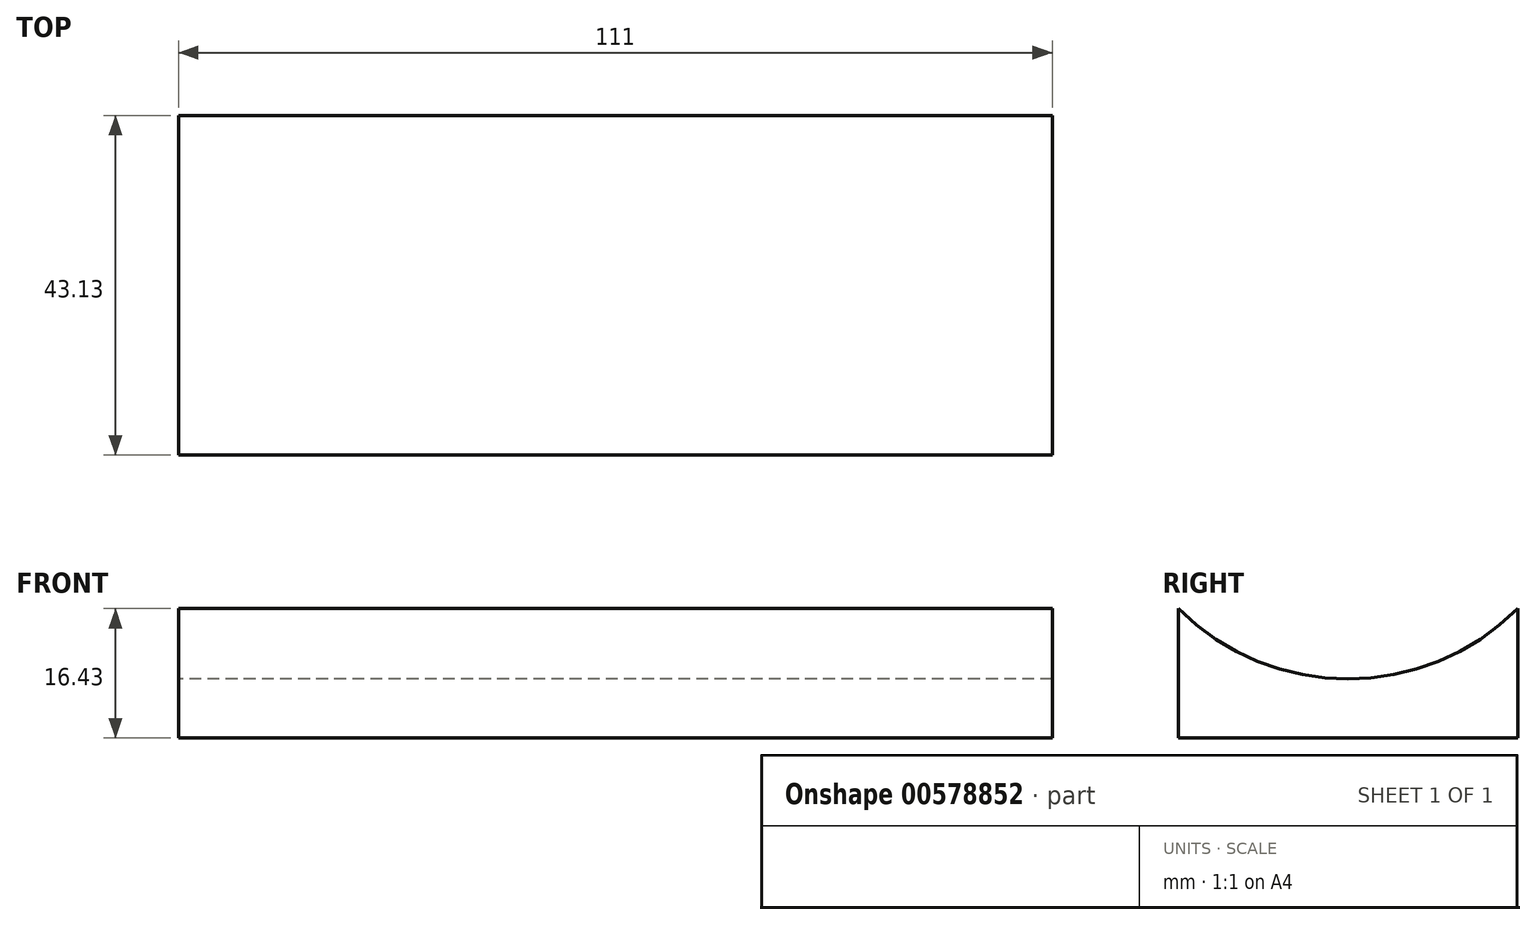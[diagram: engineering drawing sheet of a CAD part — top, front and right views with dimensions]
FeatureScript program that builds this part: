
annotation { "Feature Type Name" : "Feature", "Feature Type Description" : "" }
export const myFeature = defineFeature(function(context is Context, id is Id, definition is map)
    precondition{}
    {
        {
            var Q0;
            Q0=qCreatedBy(makeId("Right.planeOp"),FACE);
            var sketch = newSketch(context, id + "F0", { "sketchPlane" : qUnion([Q0])});
            skLineSegment(sketch, "E0.bottom", {"start": v(0, 0) * mm, "end": v(43.13, 0) * mm});
            skLineSegment(sketch, "E0.left", {"start": v(0, 0) * mm, "end": v(0, 16.43) * mm});
            skLineSegment(sketch, "E0.right", {"start": v(43.13, 0) * mm, "end": v(43.13, 16.43) * mm});
            skArc(sketch, "E1", {"start": v(0, 16.43) * mm, "mid": v(21.57, 7.5) * mm, "end": v(43.13, 16.43) * mm});
            skLineSegment(sketch, "E2", {"start": v(0, 16.43) * mm, "end": v(21.57, 38) * mm, "construction": true});
            skLineSegment(sketch, "E3", {"start": v(43.13, 16.43) * mm, "end": v(21.57, 38) * mm, "construction": true});
            skLineSegment(sketch, "E4", {"start": v(21.57, 38) * mm, "end": v(21.57, 7.5) * mm, "construction": true});
            skCircle(sketch, "E5.cCircle", {"center": v(21.57, 38) * mm, "radius": 31 * mm, "construction": true});
            skLineSegment(sketch, "E5.0", {"start": v(21.57, 7) * mm, "end": v(-5.28, 22.5) * mm, "construction": true});
            skLineSegment(sketch, "E5.1", {"start": v(-5.28, 22.5) * mm, "end": v(-5.28, 53.5) * mm, "construction": true});
            skLineSegment(sketch, "E5.2", {"start": v(-5.28, 53.5) * mm, "end": v(21.57, 69) * mm, "construction": true});
            skLineSegment(sketch, "E5.3", {"start": v(21.57, 69) * mm, "end": v(48.41, 53.5) * mm, "construction": true});
            skLineSegment(sketch, "E5.4", {"start": v(48.41, 53.5) * mm, "end": v(48.41, 22.5) * mm, "construction": true});
            skLineSegment(sketch, "E5.5", {"start": v(48.41, 22.5) * mm, "end": v(21.57, 7) * mm, "construction": true});
            skCircle(sketch, "E6", {"center": v(21.57, 38) * mm, "radius": 37.5 * mm, "construction": true});
            skSolve(sketch);
        }
        {
            var Q0;
            Q0 = qSketchRegion(id + "F0", true);
            extrude(context, id + "F1", {"entities" : qUnion([Q0]), "depth" : 111 * mm, "offsetDistance" : 25 * mm});
        }
    });
